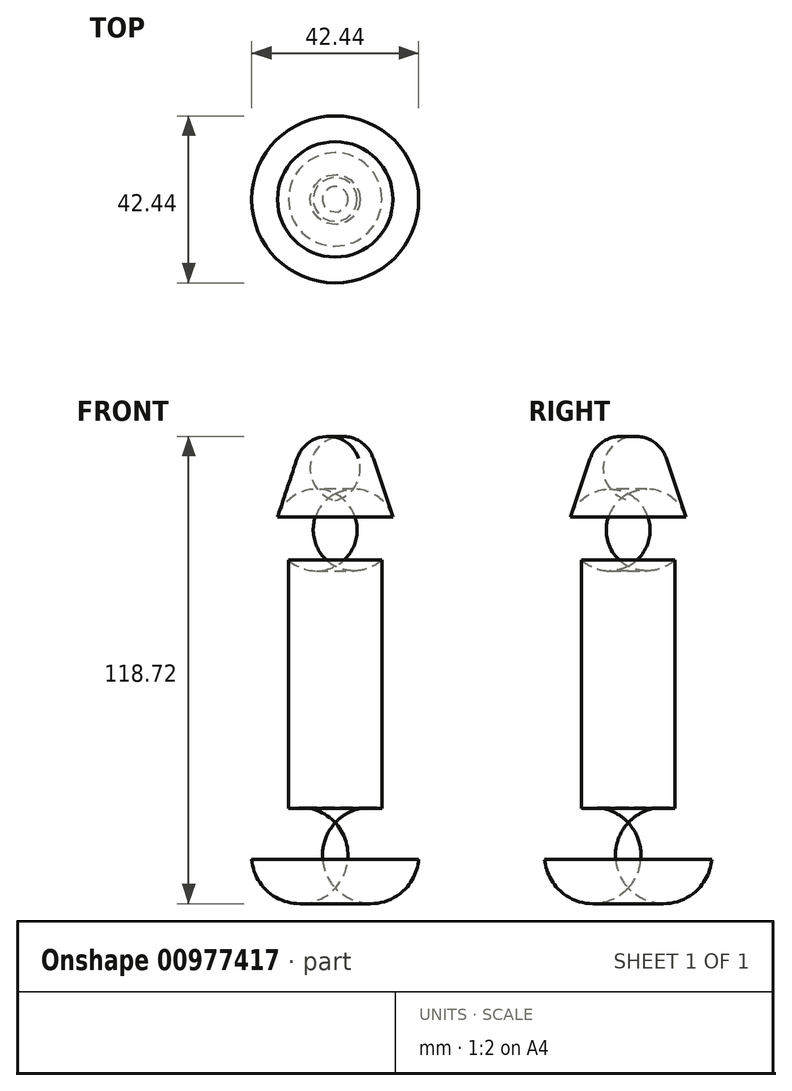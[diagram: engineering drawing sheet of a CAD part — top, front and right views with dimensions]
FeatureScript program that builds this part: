
annotation { "Feature Type Name" : "Feature", "Feature Type Description" : "" }
export const myFeature = defineFeature(function(context is Context, id is Id, definition is map)
    precondition{}
    {
        {
            var Q0;
            Q0=qCreatedBy(makeId("Front.planeOp"),FACE);
            var sketch = newSketch(context, id + "F0", { "sketchPlane" : qUnion([Q0])});
            skLineSegment(sketch, "E0", {"start": v(-9.68, 52.54) * mm, "end": v(-14.65, 37.68) * mm});
            skLineSegment(sketch, "E1", {"start": v(-11.85, 26.76) * mm, "end": v(-11.85, -36.39) * mm});
            skArc(sketch, "E2", {"start": v(-11.85, -36.39) * mm, "mid": v(-18.9, -41.09) * mm, "end": v(-21.22, -49.24) * mm});
            skArc(sketch, "E3", {"start": v(-14.65, 37.68) * mm, "mid": v(-14.86, 31.8) * mm, "end": v(-11.85, 26.76) * mm});
            skArc(sketch, "E4", {"start": v(0, 57.95) * mm, "mid": v(-5.89, 57.12) * mm, "end": v(-9.68, 52.54) * mm});
            skLineSegment(sketch, "E5", {"start": v(-21.22, -49.24) * mm, "end": v(0, -49.24) * mm});
            skLineSegment(sketch, "E6", {"start": v(0, -49.24) * mm, "end": v(0, 57.95) * mm});
            skSolve(sketch);
        }
        {
            var Q0;
            Q0 = qSketchRegion(id + "F0", true);
            var Q1;
            Q1=sQuery(id+"F0.wireOp",EDGE,"E6");
            revolve(context, id + "F1", {"surfaceOperationType" : NewSurfaceOperationType.NEW, "entities" : qUnion([Q0]), "axis" : qUnion([Q1]), "revolveType" : RevolveType.FULL});
        }
    });
